# Revit family: WST_A3-C2FH
name_source: partatom
category: Windows
revit_build: Autodesk Revit 2016 (Build: 20150220_1215(x64)
units: mm (PartAtom-declared; Revit-internal decimal feet)

## family parameters
Always vertical = Yes
Cut with Voids When Loaded = No
Host = Wall
Room Calculation Point = No
Shared = No

## types (1)
- C2FH Durowin
    Assembly Code = B2020120
    Construction Type = Steel
    Head Height = 2125 mm  [stored 6.97178 ft]
    Height = 949 mm
    Inset = 110 mm
    Manufacturer = Durowin
    Manufacturer Code = C2FH
    Material frame = Default Steel frame
    Material glass = Glass
    Model = C Type Residential open out
    Model Type = C TYPE
    URL = http://www.durowin.comswartland.co.za
    Wall Closure = By host
    Width = 1022 mm  [stored 3.35302 ft]

note: [stored X ft] marks values corroborated as IEEE doubles in the binary element streams (Revit-internal decimal feet)

## geometry (parser evidence)
native form markers: Sweep x14
no freeform markers — native parametric forms only
